# Revit family: 2055135 Lighting Fixture_Sylvania_Glace Pendant_Ceiling Pendant
name_source: partatom
category: Lighting Fixtures
revit_build: Autodesk Revit 2017 (Build: 20190507_1515(x64)
units: mm (PartAtom-declared; Revit-internal decimal feet)

## family parameters
Cut with Voids When Loaded = No
Host = Face
Light Source = Yes
OmniClass Number = 23.80.70.11.17
OmniClass Title = Specialized Lighting by Location or Use
Part Type = Normal
Room Calculation Point = No
Round Connector Dimension = Use Diameter
Shared = No

## types (1)
- Glace Pend 3K DALI HO Rnd
    Accessory Material = Metal_Sylvania_Glace_Chrome
    Apparent Load = 20 VA
    Assembly Code = D5020200
    Body Marerial = Aluminum_Sylvania_Glace_Silver
    Cable Material = Rubber_Sylvania_Glace_Gray
    Catalog Number = 2055135 Glace Pend 4K DALI HO Rnd
    Color Filter = 16777215
    Default Elevation = 0 mm  [stored 0 ft]
    Description = Super slim architectural design provides ultra modern minimalism with cutting-edge LED technology Utilises low power super efficient LED array providing perfect homogenous light distribution Superior fixture lumens Aesthetic architectural form Pendant version 50,000 hrs life at 70% of the original output L70 Integral LED emergency options DALI dimming versions as standard Integral diffuser
    Diameter = 240 mm  [stored 0.787402 ft]
    Diffuser Diameter = 400 mm  [stored 1.31234 ft]
    Diffuser Material = Acrylic_Sylvania_Glace_Opal
    Dimming Lamp Color Temperature Shift = <None>
    Dimming Range = 5%-100%
    Drive Current = 700 mA
    Emit Shape Visible in Rendering = Yes
    Emit from Circle Diameter = 190 mm
    Energy Class = A++,A+,A
    Height = 54 mm  [stored 0.177165 ft]
    IK Rating = IK02
    IP Rating = IP20
    LOR = 100 %
    Lamp = Integrated LED
    Lamp Comments = 1 x 20W
    Life = 50 000 h
    Manufacturer = Feilo Sylvania
    Model = Glace Pend 4K DALI HO Rnd
    Mounting Height = 1000 mm  [stored 3.28084 ft]
    Mounting Radius = 50 mm  [stored 0.164042 ft]
    Photometric Web File = 2055135_GlacePend4KDALIHORnd-192620.ies
    Product Family = GLACE PENDANT
    Product Page URL = http://www.sylvania-lighting.com
    Tilt Angle = -90°
    URL = http://www.sylvania-lighting.com
    Voltage = 230 V
    Voltage Comments = UNV (Universal Voltage; 220-240 Volt)
    Weight = 2 kg

note: [stored X ft] marks values corroborated as IEEE doubles in the binary element streams (Revit-internal decimal feet)

## geometry (parser evidence)
native form markers: Blend x6, Sweep x1
no freeform markers — native parametric forms only
